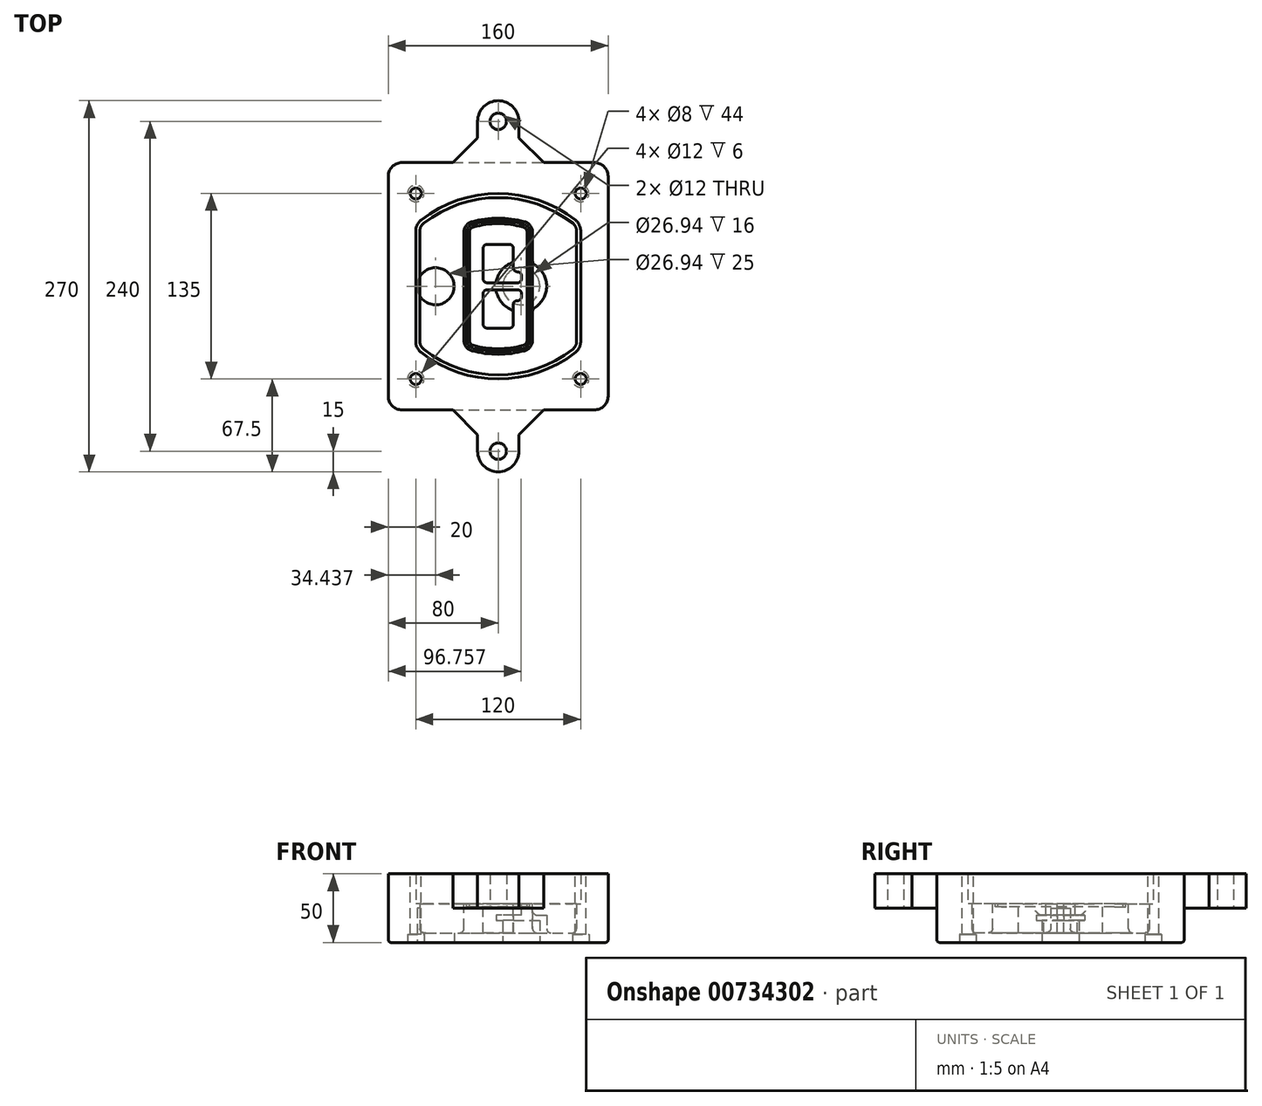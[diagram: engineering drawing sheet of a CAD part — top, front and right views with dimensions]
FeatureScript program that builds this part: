
annotation { "Feature Type Name" : "Feature", "Feature Type Description" : "" }
export const myFeature = defineFeature(function(context is Context, id is Id, definition is map)
    precondition{}
    {
        {
            var Q0;
            Q0=qCreatedBy(makeId("Top.planeOp"),FACE);
            var sketch = newSketch(context, id + "F0", { "sketchPlane" : qUnion([Q0])});
            skPoint(sketch, "E0.rect.middle", {"position": v(0, 0) * mm});
            skLineSegment(sketch, "E1.bottom", {"start": v(-70, -90) * mm, "end": v(70, -90) * mm});
            skLineSegment(sketch, "E1.top", {"start": v(-70, 90) * mm, "end": v(70, 90) * mm});
            skLineSegment(sketch, "E1.left", {"start": v(-80, -80) * mm, "end": v(-80, 80) * mm});
            skLineSegment(sketch, "E1.right", {"start": v(80, -80) * mm, "end": v(80, 80) * mm});
            skLineSegment(sketch, "E2", {"start": v(-80, 90) * mm, "end": v(80, -90) * mm, "construction": true});
            skLineSegment(sketch, "E3", {"start": v(80, 90) * mm, "end": v(-80, -90) * mm, "construction": true});
            skCircle(sketch, "E4", {"center": v(-60, 67.5) * mm, "radius": 4 * mm});
            skCircle(sketch, "E5", {"center": v(60, 67.5) * mm, "radius": 4 * mm});
            skCircle(sketch, "E6", {"center": v(60, -67.5) * mm, "radius": 4 * mm});
            skCircle(sketch, "E7", {"center": v(-60, -67.5) * mm, "radius": 4 * mm});
            skLineSegment(sketch, "E8", {"start": v(-60, 67.5) * mm, "end": v(60, 67.5) * mm, "construction": true});
            skLineSegment(sketch, "E9", {"start": v(60, 67.5) * mm, "end": v(60, -67.5) * mm, "construction": true});
            skLineSegment(sketch, "E10", {"start": v(60, -67.5) * mm, "end": v(-60, -67.5) * mm, "construction": true});
            skLineSegment(sketch, "E11", {"start": v(-60, -67.5) * mm, "end": v(-60, 67.5) * mm, "construction": true});
            skLineSegment(sketch, "E12", {"start": v(-60, 40.3) * mm, "end": v(-60, -40.3) * mm});
            skLineSegment(sketch, "E13", {"start": v(60, 40.3) * mm, "end": v(60, -40.3) * mm});
            skArc(sketch, "E14", {"start": v(56.15, 48.18) * mm, "mid": v(0, 67.5) * mm, "end": v(-56.15, 48.18) * mm});
            skArc(sketch, "E15", {"start": v(-56.15, -48.18) * mm, "mid": v(0, -67.5) * mm, "end": v(56.15, -48.18) * mm});
            skLineSegment(sketch, "E16", {"start": v(-60, 0) * mm, "end": v(60, 0) * mm, "construction": true});
            skPoint(sketch, "E17.visualSharp", {"position": v(-60, -45) * mm});
            skArc(sketch, "E17.filletArc", {"start": v(-60, -40.3) * mm, "mid": v(-58.99, -44.68) * mm, "end": v(-56.15, -48.18) * mm});
            skPoint(sketch, "E18.visualSharp", {"position": v(-60, 45) * mm});
            skArc(sketch, "E18.filletArc", {"start": v(-56.15, 48.18) * mm, "mid": v(-58.99, 44.68) * mm, "end": v(-60, 40.3) * mm});
            skPoint(sketch, "E19.visualSharp", {"position": v(60, 45) * mm});
            skArc(sketch, "E19.filletArc", {"start": v(60, 40.3) * mm, "mid": v(58.99, 44.68) * mm, "end": v(56.15, 48.18) * mm});
            skPoint(sketch, "E20.visualSharp", {"position": v(60, -45) * mm});
            skArc(sketch, "E20.filletArc", {"start": v(56.15, -48.18) * mm, "mid": v(58.99, -44.68) * mm, "end": v(60, -40.3) * mm});
            skPoint(sketch, "E21.visualSharp", {"position": v(-80, 90) * mm});
            skArc(sketch, "E21.filletArc", {"start": v(-70, 90) * mm, "mid": v(-77.07, 87.07) * mm, "end": v(-80, 80) * mm});
            skPoint(sketch, "E22.visualSharp", {"position": v(80, 90) * mm});
            skArc(sketch, "E22.filletArc", {"start": v(80, 80) * mm, "mid": v(77.07, 87.07) * mm, "end": v(70, 90) * mm});
            skPoint(sketch, "E23.visualSharp", {"position": v(80, -90) * mm});
            skArc(sketch, "E23.filletArc", {"start": v(70, -90) * mm, "mid": v(77.07, -87.07) * mm, "end": v(80, -80) * mm});
            skPoint(sketch, "E24.visualSharp", {"position": v(-80, -90) * mm});
            skArc(sketch, "E24.filletArc", {"start": v(-80, -80) * mm, "mid": v(-77.07, -87.07) * mm, "end": v(-70, -90) * mm});
            skArc(sketch, "E25.0", {"start": v(57, 40.3) * mm, "mid": v(56.3, 43.36) * mm, "end": v(54.3, 45.81) * mm});
            skLineSegment(sketch, "E25.1", {"start": v(57, 40.3) * mm, "end": v(57, -40.3) * mm});
            skArc(sketch, "E25.2", {"start": v(54.3, -45.81) * mm, "mid": v(56.3, -43.36) * mm, "end": v(57, -40.3) * mm});
            skArc(sketch, "E25.3", {"start": v(-54.3, -45.81) * mm, "mid": v(0, -64.5) * mm, "end": v(54.3, -45.81) * mm});
            skArc(sketch, "E25.4", {"start": v(-57, -40.3) * mm, "mid": v(-56.3, -43.36) * mm, "end": v(-54.3, -45.81) * mm});
            skArc(sketch, "E25.5", {"start": v(54.3, 45.81) * mm, "mid": v(0, 64.5) * mm, "end": v(-54.3, 45.81) * mm});
            skLineSegment(sketch, "E25.6", {"start": v(-57, 40.3) * mm, "end": v(-57, -40.3) * mm});
            skArc(sketch, "E25.7", {"start": v(-54.3, 45.81) * mm, "mid": v(-56.3, 43.36) * mm, "end": v(-57, 40.3) * mm});
            skArc(sketch, "E26.0", {"start": v(-58.62, 51.33) * mm, "mid": v(-62.58, 46.43) * mm, "end": v(-64, 40.3) * mm});
            skArc(sketch, "E26.1", {"start": v(58.62, 51.33) * mm, "mid": v(0, 71.5) * mm, "end": v(-58.62, 51.33) * mm});
            skArc(sketch, "E26.2", {"start": v(64, 40.3) * mm, "mid": v(62.58, 46.43) * mm, "end": v(58.62, 51.33) * mm});
            skLineSegment(sketch, "E26.3", {"start": v(64, 40.3) * mm, "end": v(64, -40.3) * mm});
            skArc(sketch, "E26.4", {"start": v(58.62, -51.33) * mm, "mid": v(62.58, -46.43) * mm, "end": v(64, -40.3) * mm});
            skLineSegment(sketch, "E26.5", {"start": v(-64, 40.3) * mm, "end": v(-64, -40.3) * mm});
            skArc(sketch, "E26.6", {"start": v(-58.62, -51.33) * mm, "mid": v(0, -71.5) * mm, "end": v(58.62, -51.33) * mm});
            skArc(sketch, "E26.7", {"start": v(-64, -40.3) * mm, "mid": v(-62.58, -46.43) * mm, "end": v(-58.62, -51.33) * mm});
            skSolve(sketch);
        }
        {
            var Q0;
            Q0=makeQuery(id+"F0.imprint","IMPRINT",FACE,{"disambiguationData":[TD([[makeQuery(id+"F0.imprint","IMPRINT",EDGE,{"derivedFrom":sQuery(id+"F0.wireOp",EDGE,"E1.bottom")}),1.0]])]});
            var Q1;
            Q1=makeQuery(id+"F0.imprint","IMPRINT",FACE,{"disambiguationData":[TD([[makeQuery(id+"F0.imprint","IMPRINT",EDGE,{"derivedFrom":sQuery(id+"F0.wireOp",EDGE,"E12")}),1.0]])]});
            var Q2;
            Q2=makeQuery(id+"F0.imprint","IMPRINT",FACE,{"disambiguationData":[TD([[makeQuery(id+"F0.imprint","IMPRINT",EDGE,{"derivedFrom":sQuery(id+"F0.wireOp",EDGE,"E25.0")}),1.0]])]});
            var Q3;
            Q3=makeQuery(id+"F0.imprint","IMPRINT",FACE,{"disambiguationData":[TD([[makeQuery(id+"F0.imprint","IMPRINT",EDGE,{"derivedFrom":sQuery(id+"F0.wireOp",EDGE,"E12")}),-1.0]])]});
            extrude(context, id + "F1", {"entities" : qUnion([Q0, Q1, Q2, Q3]), "oppositeDirection" : true, "depth" : 25 * mm});
        }
        {
            var Q0;
            Q0=makeQuery(id+"F0.imprint","IMPRINT",FACE,{"disambiguationData":[TD([[makeQuery(id+"F0.imprint","IMPRINT",EDGE,{"derivedFrom":sQuery(id+"F0.wireOp",EDGE,"E12")}),1.0]])]});
            extrude(context, id + "F2", {"entities" : qUnion([Q0]), "operationType" : NewBodyOperationType.ADD, "depth" : 3 * mm});
        }
        {
            var Q0;
            Q0=makeQuery(id+"F0.imprint","IMPRINT",FACE,{"disambiguationData":[TD([[makeQuery(id+"F0.imprint","IMPRINT",EDGE,{"derivedFrom":sQuery(id+"F0.wireOp",EDGE,"E25.0")}),1.0]])]});
            extrude(context, id + "F3", {"entities" : qUnion([Q0]), "operationType" : NewBodyOperationType.REMOVE, "oppositeDirection" : true, "depth" : 18 * mm});
        }
        {
            var Q0;
            Q0=makeQuery(id+"F2.opExtrude","CAP_FACE",FACE,{"disambiguationData":[OSD([sQuery(id+"F0.wireOp",EDGE,"E12"),sQuery(id+"F0.wireOp",EDGE,"E13"),sQuery(id+"F0.wireOp",EDGE,"E14"),sQuery(id+"F0.wireOp",EDGE,"E15"),sQuery(id+"F0.wireOp",EDGE,"E17.filletArc"),sQuery(id+"F0.wireOp",EDGE,"E18.filletArc"),sQuery(id+"F0.wireOp",EDGE,"E19.filletArc"),sQuery(id+"F0.wireOp",EDGE,"E20.filletArc"),sQuery(id+"F0.wireOp",EDGE,"E25.0"),sQuery(id+"F0.wireOp",EDGE,"E25.1"),sQuery(id+"F0.wireOp",EDGE,"E25.2"),sQuery(id+"F0.wireOp",EDGE,"E25.3"),sQuery(id+"F0.wireOp",EDGE,"E25.4"),sQuery(id+"F0.wireOp",EDGE,"E25.5"),sQuery(id+"F0.wireOp",EDGE,"E25.6"),sQuery(id+"F0.wireOp",EDGE,"E25.7")])],"isStart":false});
            var sketch = newSketch(context, id + "F4", { "sketchPlane" : qUnion([Q0])});
            skArc(sketch, "E27.0", {"start": v(-19.08, -46.97) * mm, "mid": v(0, -49.5) * mm, "end": v(19.08, -46.97) * mm});
            skArc(sketch, "E28.0", {"start": v(19.08, 46.97) * mm, "mid": v(0, 49.5) * mm, "end": v(-19.08, 46.97) * mm});
            skLineSegment(sketch, "E29", {"start": v(-25, 39.25) * mm, "end": v(-25, -39.25) * mm});
            skLineSegment(sketch, "E30", {"start": v(25, 39.25) * mm, "end": v(25, -39.25) * mm});
            skLineSegment(sketch, "E31", {"start": v(-25, 45.1) * mm, "end": v(25, 45.1) * mm, "construction": true});
            skLineSegment(sketch, "E32", {"start": v(-25, -45.1) * mm, "end": v(25, -45.1) * mm, "construction": true});
            skPoint(sketch, "E33.visualSharp", {"position": v(-25, 45.1) * mm});
            skArc(sketch, "E33.filletArc", {"start": v(-19.08, 46.97) * mm, "mid": v(-23.35, 44.11) * mm, "end": v(-25, 39.25) * mm});
            skPoint(sketch, "E34.visualSharp", {"position": v(25, 45.1) * mm});
            skArc(sketch, "E34.filletArc", {"start": v(25, 39.25) * mm, "mid": v(23.35, 44.11) * mm, "end": v(19.08, 46.97) * mm});
            skPoint(sketch, "E35.visualSharp", {"position": v(25, -45.1) * mm});
            skArc(sketch, "E35.filletArc", {"start": v(19.08, -46.97) * mm, "mid": v(23.35, -44.11) * mm, "end": v(25, -39.25) * mm});
            skPoint(sketch, "E36.visualSharp", {"position": v(-25, -45.1) * mm});
            skArc(sketch, "E36.filletArc", {"start": v(-25, -39.25) * mm, "mid": v(-23.35, -44.11) * mm, "end": v(-19.08, -46.97) * mm});
            skArc(sketch, "E37.0", {"start": v(54.3, 45.81) * mm, "mid": v(0, 64.5) * mm, "end": v(-54.3, 45.81) * mm});
            skArc(sketch, "E37.1", {"start": v(-54.3, 45.81) * mm, "mid": v(-56.3, 43.36) * mm, "end": v(-57, 40.3) * mm});
            skLineSegment(sketch, "E37.2", {"start": v(-57, 40.3) * mm, "end": v(-57, -40.3) * mm});
            skArc(sketch, "E37.3", {"start": v(-57, -40.3) * mm, "mid": v(-56.3, -43.36) * mm, "end": v(-54.3, -45.81) * mm});
            skArc(sketch, "E37.4", {"start": v(-54.3, -45.81) * mm, "mid": v(0, -64.5) * mm, "end": v(54.3, -45.81) * mm});
            skArc(sketch, "E37.5", {"start": v(54.3, -45.81) * mm, "mid": v(56.3, -43.36) * mm, "end": v(57, -40.3) * mm});
            skLineSegment(sketch, "E37.6", {"start": v(57, 40.3) * mm, "end": v(57, -40.3) * mm});
            skArc(sketch, "E37.7", {"start": v(57, 40.3) * mm, "mid": v(56.3, 43.36) * mm, "end": v(54.3, 45.81) * mm});
            skLineSegment(sketch, "E38.0", {"start": v(23, 39.25) * mm, "end": v(23, -39.25) * mm});
            skArc(sketch, "E38.1", {"start": v(18.56, -45.04) * mm, "mid": v(21.76, -42.9) * mm, "end": v(23, -39.25) * mm});
            skArc(sketch, "E38.2", {"start": v(-18.56, -45.04) * mm, "mid": v(0, -47.5) * mm, "end": v(18.56, -45.04) * mm});
            skArc(sketch, "E38.3", {"start": v(-23, -39.25) * mm, "mid": v(-21.76, -42.9) * mm, "end": v(-18.56, -45.04) * mm});
            skLineSegment(sketch, "E38.4", {"start": v(-23, 39.25) * mm, "end": v(-23, -39.25) * mm});
            skArc(sketch, "E38.5", {"start": v(23, 39.25) * mm, "mid": v(21.76, 42.9) * mm, "end": v(18.56, 45.04) * mm});
            skArc(sketch, "E38.6", {"start": v(-18.56, 45.04) * mm, "mid": v(-21.76, 42.9) * mm, "end": v(-23, 39.25) * mm});
            skArc(sketch, "E38.7", {"start": v(18.56, 45.04) * mm, "mid": v(0, 47.5) * mm, "end": v(-18.56, 45.04) * mm});
            skArc(sketch, "E39.0", {"start": v(21, 39.25) * mm, "mid": v(20.18, 41.68) * mm, "end": v(18.04, 43.1) * mm});
            skLineSegment(sketch, "E39.1", {"start": v(21, 39.25) * mm, "end": v(21, -39.25) * mm});
            skArc(sketch, "E39.2", {"start": v(18.04, -43.1) * mm, "mid": v(20.18, -41.68) * mm, "end": v(21, -39.25) * mm});
            skArc(sketch, "E39.3", {"start": v(-18.04, -43.1) * mm, "mid": v(0, -45.5) * mm, "end": v(18.04, -43.1) * mm});
            skArc(sketch, "E39.4", {"start": v(-21, -39.25) * mm, "mid": v(-20.18, -41.68) * mm, "end": v(-18.04, -43.1) * mm});
            skArc(sketch, "E39.5", {"start": v(18.04, 43.1) * mm, "mid": v(0, 45.5) * mm, "end": v(-18.04, 43.1) * mm});
            skLineSegment(sketch, "E39.6", {"start": v(-21, 39.25) * mm, "end": v(-21, -39.25) * mm});
            skArc(sketch, "E39.7", {"start": v(-18.04, 43.1) * mm, "mid": v(-20.18, 41.68) * mm, "end": v(-21, 39.25) * mm});
            skLineSegment(sketch, "E40", {"start": v(-25, 0) * mm, "end": v(25, 0) * mm, "construction": true});
            skLineSegment(sketch, "E41", {"start": v(-11, 5.5) * mm, "end": v(-11, 27.5) * mm});
            skLineSegment(sketch, "E42", {"start": v(-8, 30.5) * mm, "end": v(8, 30.5) * mm});
            skLineSegment(sketch, "E43", {"start": v(11, 27.5) * mm, "end": v(11, 13.5) * mm});
            skLineSegment(sketch, "E44", {"start": v(14, 10.5) * mm, "end": v(14, 10.5) * mm});
            skLineSegment(sketch, "E45", {"start": v(17, 7.5) * mm, "end": v(17, 5.5) * mm});
            skLineSegment(sketch, "E46", {"start": v(14, 2.5) * mm, "end": v(-8, 2.5) * mm});
            skPoint(sketch, "E47.visualSharp", {"position": v(-11, 30.5) * mm});
            skArc(sketch, "E47.filletArc", {"start": v(-8, 30.5) * mm, "mid": v(-10.12, 29.62) * mm, "end": v(-11, 27.5) * mm});
            skPoint(sketch, "E48.visualSharp", {"position": v(11, 30.5) * mm});
            skArc(sketch, "E48.filletArc", {"start": v(11, 27.5) * mm, "mid": v(10.12, 29.62) * mm, "end": v(8, 30.5) * mm});
            skPoint(sketch, "E49.visualSharp", {"position": v(11, 10.5) * mm});
            skArc(sketch, "E49.filletArc", {"start": v(11, 13.5) * mm, "mid": v(11.88, 11.38) * mm, "end": v(14, 10.5) * mm});
            skPoint(sketch, "E50.visualSharp", {"position": v(17, 10.5) * mm});
            skArc(sketch, "E50.filletArc", {"start": v(17, 7.5) * mm, "mid": v(16.12, 9.62) * mm, "end": v(14, 10.5) * mm});
            skPoint(sketch, "E51.visualSharp", {"position": v(17, 2.5) * mm});
            skArc(sketch, "E51.filletArc", {"start": v(14, 2.5) * mm, "mid": v(16.12, 3.38) * mm, "end": v(17, 5.5) * mm});
            skPoint(sketch, "E52.visualSharp", {"position": v(-11, 2.5) * mm});
            skArc(sketch, "E52.filletArc", {"start": v(-11, 5.5) * mm, "mid": v(-10.12, 3.38) * mm, "end": v(-8, 2.5) * mm});
            skLineSegment(sketch, "E53.0.MirrorCS", {"start": v(14, -2.5) * mm, "end": v(-8, -2.5) * mm});
            skArc(sketch, "E54.0.MirrorCS", {"start": v(-11, -5.5) * mm, "mid": v(-10.12, -3.38) * mm, "end": v(-8, -2.5) * mm});
            skLineSegment(sketch, "E55.0.MirrorCS", {"start": v(-11, -5.5) * mm, "end": v(-11, -27.5) * mm});
            skArc(sketch, "E56.0.MirrorCS", {"start": v(-8, -30.5) * mm, "mid": v(-10.12, -29.62) * mm, "end": v(-11, -27.5) * mm});
            skLineSegment(sketch, "E57.0.MirrorCS", {"start": v(-8, -30.5) * mm, "end": v(8, -30.5) * mm});
            skArc(sketch, "E58.0.MirrorCS", {"start": v(11, -27.5) * mm, "mid": v(10.12, -29.62) * mm, "end": v(8, -30.5) * mm});
            skLineSegment(sketch, "E59.0.MirrorCS", {"start": v(11, -27.5) * mm, "end": v(11, -13.5) * mm});
            skArc(sketch, "E60.0.MirrorCS", {"start": v(11, -13.5) * mm, "mid": v(11.88, -11.38) * mm, "end": v(14, -10.5) * mm});
            skArc(sketch, "E61.0.MirrorCS", {"start": v(17, -7.5) * mm, "mid": v(16.12, -9.62) * mm, "end": v(14, -10.5) * mm});
            skLineSegment(sketch, "E62.0.MirrorCS", {"start": v(17, -7.5) * mm, "end": v(17, -5.5) * mm});
            skArc(sketch, "E63.0.MirrorCS", {"start": v(14, -2.5) * mm, "mid": v(16.12, -3.38) * mm, "end": v(17, -5.5) * mm});
            skSolve(sketch);
        }
        {
            var Q0;
            Q0=makeQuery(id+"F4.imprint","IMPRINT",FACE,{"disambiguationData":[TD([[makeQuery(id+"F4.imprint","IMPRINT",EDGE,{"derivedFrom":sQuery(id+"F4.wireOp",EDGE,"E27.0")}),1.0]])]});
            var Q1;
            Q1=makeQuery(id+"F4.imprint","IMPRINT",FACE,{"disambiguationData":[TD([[makeQuery(id+"F4.imprint","IMPRINT",EDGE,{"derivedFrom":sQuery(id+"F4.wireOp",EDGE,"E38.0")}),-1.0]])]});
            var Q2;
            Q2=makeQuery(id+"F4.imprint","IMPRINT",FACE,{"disambiguationData":[TD([[makeQuery(id+"F4.imprint","IMPRINT",EDGE,{"derivedFrom":sQuery(id+"F4.wireOp",EDGE,"E39.0")}),1.0]])]});
            extrude(context, id + "F5", {"entities" : qUnion([Q0, Q1, Q2]), "operationType" : NewBodyOperationType.ADD, "endBound" : BoundingType.UP_TO_NEXT, "oppositeDirection" : true, "depth" : 25 * mm});
        }
        {
            var Q0;
            Q0=makeQuery(id+"F4.imprint","IMPRINT",FACE,{"disambiguationData":[TD([[makeQuery(id+"F4.imprint","IMPRINT",EDGE,{"derivedFrom":sQuery(id+"F4.wireOp",EDGE,"E38.0")}),-1.0]])]});
            extrude(context, id + "F6", {"entities" : qUnion([Q0]), "operationType" : NewBodyOperationType.REMOVE, "oppositeDirection" : true, "depth" : 2 * mm});
        }
        {
            var Q0;
            Q0=makeQuery(id+"F1.opExtrude","CAP_FACE",FACE,{"disambiguationData":[OSD([sQuery(id+"F0.wireOp",EDGE,"E1.bottom"),sQuery(id+"F0.wireOp",EDGE,"E1.top"),sQuery(id+"F0.wireOp",EDGE,"E1.left"),sQuery(id+"F0.wireOp",EDGE,"E1.right"),sQuery(id+"F0.wireOp",EDGE,"E4"),sQuery(id+"F0.wireOp",EDGE,"E5"),sQuery(id+"F0.wireOp",EDGE,"E6"),sQuery(id+"F0.wireOp",EDGE,"E7"),sQuery(id+"F0.wireOp",EDGE,"E21.filletArc"),sQuery(id+"F0.wireOp",EDGE,"E22.filletArc"),sQuery(id+"F0.wireOp",EDGE,"E23.filletArc"),sQuery(id+"F0.wireOp",EDGE,"E24.filletArc")])],"isStart":false});
            var sketch = newSketch(context, id + "F7", { "sketchPlane" : qUnion([Q0])});
            skCircle(sketch, "E64", {"center": v(16.76, 0) * mm, "radius": 13.47 * mm});
            skCircle(sketch, "E65", {"center": v(-45.56, 0) * mm, "radius": 13.47 * mm});
            skLineSegment(sketch, "E66", {"start": v(80, 0) * mm, "end": v(-80, 0) * mm});
            skCircle(sketch, "E67", {"center": v(16.76, 0) * mm, "radius": 18.47 * mm});
            skCircle(sketch, "E68", {"center": v(60, -67.5) * mm, "radius": 6 * mm});
            skCircle(sketch, "E69", {"center": v(-60, -67.5) * mm, "radius": 6 * mm});
            skCircle(sketch, "E70", {"center": v(-60, 67.5) * mm, "radius": 6 * mm});
            skCircle(sketch, "E71", {"center": v(60, 67.5) * mm, "radius": 6 * mm});
            skSolve(sketch);
        }
        {
            var Q0;
            {var subQ1=sQuery(id+"F7.wireOp",EDGE,"E66");var subQ4=sQuery(id+"F7.wireOp",EDGE,"E64");var subQ6=makeQuery(id+"F7.imprint","INTERSECT",VERTEX,{"disambiguationData":[OD(0.0)],"derivedFrom":[subQ4,subQ1]});Q0=makeQuery(id+"F7.imprint","IMPRINT",FACE,{"disambiguationData":[TD([[makeQuery(id+"F7.imprint","IMPRINT",EDGE,{"disambiguationData":[TD([[subQ6,-1.0]])],"derivedFrom":subQ4}),-1.0]])]});}
            var Q1;
            {var subQ0=sQuery(id+"F7.wireOp",EDGE,"E66");var subQ1=sQuery(id+"F7.wireOp",EDGE,"E64");var subQ3=makeQuery(id+"F7.imprint","INTERSECT",VERTEX,{"disambiguationData":[OD(0.0)],"derivedFrom":[subQ1,subQ0]});Q1=makeQuery(id+"F7.imprint","IMPRINT",FACE,{"disambiguationData":[TD([[makeQuery(id+"F7.imprint","IMPRINT",EDGE,{"disambiguationData":[TD([[subQ3,-1.0]])],"derivedFrom":subQ1}),1.0]])]});}
            var Q2;
            {var subQ0=sQuery(id+"F7.wireOp",EDGE,"E66");var subQ1=sQuery(id+"F7.wireOp",EDGE,"E64");var subQ3=makeQuery(id+"F7.imprint","INTERSECT",VERTEX,{"disambiguationData":[OD(0.0)],"derivedFrom":[subQ1,subQ0]});Q2=makeQuery(id+"F7.imprint","IMPRINT",FACE,{"disambiguationData":[TD([[makeQuery(id+"F7.imprint","IMPRINT",EDGE,{"disambiguationData":[TD([[subQ3,1.0]])],"derivedFrom":subQ1}),1.0]])]});}
            var Q3;
            {var subQ1=sQuery(id+"F7.wireOp",EDGE,"E66");var subQ4=sQuery(id+"F7.wireOp",EDGE,"E64");var subQ6=makeQuery(id+"F7.imprint","INTERSECT",VERTEX,{"disambiguationData":[OD(0.0)],"derivedFrom":[subQ4,subQ1]});Q3=makeQuery(id+"F7.imprint","IMPRINT",FACE,{"disambiguationData":[TD([[makeQuery(id+"F7.imprint","IMPRINT",EDGE,{"disambiguationData":[TD([[subQ6,1.0]])],"derivedFrom":subQ4}),-1.0]])]});}
            extrude(context, id + "F8", {"entities" : qUnion([Q0, Q1, Q2, Q3]), "operationType" : NewBodyOperationType.ADD, "oppositeDirection" : true, "depth" : 20 * mm});
        }
        {
            var Q0;
            {var subQ0=sQuery(id+"F7.wireOp",EDGE,"E66");var subQ1=sQuery(id+"F7.wireOp",EDGE,"E64");var subQ3=makeQuery(id+"F7.imprint","INTERSECT",VERTEX,{"disambiguationData":[OD(0.0)],"derivedFrom":[subQ1,subQ0]});Q0=makeQuery(id+"F7.imprint","IMPRINT",FACE,{"disambiguationData":[TD([[makeQuery(id+"F7.imprint","IMPRINT",EDGE,{"disambiguationData":[TD([[subQ3,-1.0]])],"derivedFrom":subQ1}),1.0]])]});}
            var Q1;
            {var subQ0=sQuery(id+"F7.wireOp",EDGE,"E66");var subQ1=sQuery(id+"F7.wireOp",EDGE,"E64");var subQ3=makeQuery(id+"F7.imprint","INTERSECT",VERTEX,{"disambiguationData":[OD(0.0)],"derivedFrom":[subQ1,subQ0]});Q1=makeQuery(id+"F7.imprint","IMPRINT",FACE,{"disambiguationData":[TD([[makeQuery(id+"F7.imprint","IMPRINT",EDGE,{"disambiguationData":[TD([[subQ3,1.0]])],"derivedFrom":subQ1}),1.0]])]});}
            extrude(context, id + "F9", {"entities" : qUnion([Q0, Q1]), "operationType" : NewBodyOperationType.REMOVE, "oppositeDirection" : true, "depth" : 16 * mm});
        }
        {
            var Q0;
            {var subQ0=sQuery(id+"F7.wireOp",EDGE,"E66");var subQ1=sQuery(id+"F7.wireOp",EDGE,"E65");var subQ3=makeQuery(id+"F7.imprint","INTERSECT",VERTEX,{"disambiguationData":[OD(0.0)],"derivedFrom":[subQ1,subQ0]});Q0=makeQuery(id+"F7.imprint","IMPRINT",FACE,{"disambiguationData":[TD([[makeQuery(id+"F7.imprint","IMPRINT",EDGE,{"disambiguationData":[TD([[subQ3,-1.0]])],"derivedFrom":subQ1}),1.0]])]});}
            var Q1;
            {var subQ0=sQuery(id+"F7.wireOp",EDGE,"E66");var subQ1=sQuery(id+"F7.wireOp",EDGE,"E65");var subQ3=makeQuery(id+"F7.imprint","INTERSECT",VERTEX,{"disambiguationData":[OD(0.0)],"derivedFrom":[subQ1,subQ0]});Q1=makeQuery(id+"F7.imprint","IMPRINT",FACE,{"disambiguationData":[TD([[makeQuery(id+"F7.imprint","IMPRINT",EDGE,{"disambiguationData":[TD([[subQ3,1.0]])],"derivedFrom":subQ1}),1.0]])]});}
            extrude(context, id + "F10", {"entities" : qUnion([Q0, Q1]), "operationType" : NewBodyOperationType.REMOVE, "oppositeDirection" : true, "depth" : 25 * mm});
        }
        {
            var Q0;
            Q0=makeQuery(id+"F7.imprint","IMPRINT",FACE,{"disambiguationData":[TD([[makeQuery(id+"F7.imprint","IMPRINT",EDGE,{"derivedFrom":sQuery(id+"F7.wireOp",EDGE,"E68")}),1.0]])]});
            var Q1;
            Q1=makeQuery(id+"F7.imprint","IMPRINT",FACE,{"disambiguationData":[TD([[makeQuery(id+"F7.imprint","IMPRINT",EDGE,{"derivedFrom":makeQuery(id+"F1.opExtrude","CAP_EDGE",EDGE,{"disambiguationData":[OSD([sQuery(id+"F0.wireOp",EDGE,"E5")])],"isStart":false})}),-1.0]])]});
            var Q2;
            Q2=makeQuery(id+"F7.imprint","IMPRINT",FACE,{"disambiguationData":[TD([[makeQuery(id+"F7.imprint","IMPRINT",EDGE,{"derivedFrom":sQuery(id+"F7.wireOp",EDGE,"E69")}),1.0]])]});
            var Q3;
            Q3=makeQuery(id+"F7.imprint","IMPRINT",FACE,{"disambiguationData":[TD([[makeQuery(id+"F7.imprint","IMPRINT",EDGE,{"derivedFrom":makeQuery(id+"F1.opExtrude","CAP_EDGE",EDGE,{"disambiguationData":[OSD([sQuery(id+"F0.wireOp",EDGE,"E4")])],"isStart":false})}),-1.0]])]});
            var Q4;
            Q4=makeQuery(id+"F7.imprint","IMPRINT",FACE,{"disambiguationData":[TD([[makeQuery(id+"F7.imprint","IMPRINT",EDGE,{"derivedFrom":sQuery(id+"F7.wireOp",EDGE,"E70")}),1.0]])]});
            var Q5;
            Q5=makeQuery(id+"F7.imprint","IMPRINT",FACE,{"disambiguationData":[TD([[makeQuery(id+"F7.imprint","IMPRINT",EDGE,{"derivedFrom":makeQuery(id+"F1.opExtrude","CAP_EDGE",EDGE,{"disambiguationData":[OSD([sQuery(id+"F0.wireOp",EDGE,"E7")])],"isStart":false})}),-1.0]])]});
            var Q6;
            Q6=makeQuery(id+"F7.imprint","IMPRINT",FACE,{"disambiguationData":[TD([[makeQuery(id+"F7.imprint","IMPRINT",EDGE,{"derivedFrom":sQuery(id+"F7.wireOp",EDGE,"E71")}),1.0]])]});
            var Q7;
            Q7=makeQuery(id+"F7.imprint","IMPRINT",FACE,{"disambiguationData":[TD([[makeQuery(id+"F7.imprint","IMPRINT",EDGE,{"derivedFrom":makeQuery(id+"F1.opExtrude","CAP_EDGE",EDGE,{"disambiguationData":[OSD([sQuery(id+"F0.wireOp",EDGE,"E6")])],"isStart":false})}),-1.0]])]});
            extrude(context, id + "F11", {"entities" : qUnion([Q0, Q1, Q2, Q3, Q4, Q5, Q6, Q7]), "operationType" : NewBodyOperationType.REMOVE, "oppositeDirection" : true, "depth" : 6 * mm});
        }
        {
            var Q0;
            Q0=makeQuery(id+"F9.boolean.opBoolean","COPY",FACE,{"derivedFrom":makeQuery(id+"F9.opExtrude","CAP_FACE",FACE,{"disambiguationData":[OSD([sQuery(id+"F7.wireOp",EDGE,"E64")])],"isStart":false})});
            var sketch = newSketch(context, id + "F12", { "sketchPlane" : qUnion([Q0])});
            skArc(sketch, "E72.0", {"start": v(11, 17.55) * mm, "mid": v(2.57, 11.82) * mm, "end": v(-1.54, 2.5) * mm});
            skArc(sketch, "E72.1", {"start": v(-1.54, -2.5) * mm, "mid": v(2.57, -11.82) * mm, "end": v(11, -17.55) * mm});
            skLineSegment(sketch, "E73", {"start": v(-1.54, -2.5) * mm, "end": v(14, -2.5) * mm});
            skLineSegment(sketch, "E74.0", {"start": v(14, 2.5) * mm, "end": v(-1.54, 2.5) * mm});
            skArc(sketch, "E74.1", {"start": v(14, 2.5) * mm, "mid": v(16.12, 3.38) * mm, "end": v(17, 5.5) * mm});
            skLineSegment(sketch, "E74.2", {"start": v(17, 7.5) * mm, "end": v(17, 5.5) * mm});
            skArc(sketch, "E74.3", {"start": v(17, 7.5) * mm, "mid": v(16.12, 9.62) * mm, "end": v(14, 10.5) * mm});
            skArc(sketch, "E74.4", {"start": v(11, 13.5) * mm, "mid": v(11.88, 11.38) * mm, "end": v(14, 10.5) * mm});
            skLineSegment(sketch, "E74.5", {"start": v(11, 17.55) * mm, "end": v(11, 13.5) * mm});
            skLineSegment(sketch, "E74.7", {"start": v(14, -2.5) * mm, "end": v(-1.54, -2.5) * mm});
            skArc(sketch, "E74.8", {"start": v(14, -2.5) * mm, "mid": v(16.12, -3.38) * mm, "end": v(17, -5.5) * mm});
            skLineSegment(sketch, "E74.9", {"start": v(17, -7.5) * mm, "end": v(17, -5.5) * mm});
            skArc(sketch, "E74.10", {"start": v(17, -7.5) * mm, "mid": v(16.12, -9.62) * mm, "end": v(14, -10.5) * mm});
            skArc(sketch, "E74.11", {"start": v(11, -13.5) * mm, "mid": v(11.88, -11.38) * mm, "end": v(14, -10.5) * mm});
            skLineSegment(sketch, "E74.12", {"start": v(11, -17.55) * mm, "end": v(11, -13.5) * mm});
            skPoint(sketch, "E75.orphan", {"position": v(11, -27.5) * mm});
            skPoint(sketch, "E76.orphan", {"position": v(-8, -2.5) * mm});
            skPoint(sketch, "E77.orphan", {"position": v(-8, 2.5) * mm});
            skPoint(sketch, "E78.orphan", {"position": v(11, 27.5) * mm});
            skSolve(sketch);
        }
        {
            var Q0;
            {var subQ7=sQuery(id+"F12.wireOp",EDGE,"E72.0");var subQ14=sQuery(id+"F12.wireOp",EDGE,"E72.1");var subQ16=sQuery(id+"F12.wireOp",EDGE,"E74.1");var subQ18=sQuery(id+"F12.wireOp",EDGE,"E74.8");Q0=qUnion([makeQuery(id+"F12.imprint","IMPRINT",FACE,{"disambiguationData":[TD([[makeQuery(id+"F12.imprint","IMPRINT",EDGE,{"derivedFrom":subQ7}),1.0]])]}),makeQuery(id+"F12.imprint","IMPRINT",FACE,{"disambiguationData":[TD([[makeQuery(id+"F12.imprint","IMPRINT",EDGE,{"derivedFrom":subQ14}),1.0]])]}),makeQuery(id+"F12.imprint","IMPRINT",FACE,{"disambiguationData":[TD([[makeQuery(id+"F12.imprint","IMPRINT",EDGE,{"derivedFrom":subQ16}),1.0]])]}),makeQuery(id+"F12.imprint","IMPRINT",FACE,{"disambiguationData":[TD([[makeQuery(id+"F12.imprint","IMPRINT",EDGE,{"derivedFrom":subQ18}),-1.0]])]})]);}
            var Q1;
            Q1=makeQuery(id+"F5.boolean.opBoolean","SPLIT",FACE,{"disambiguationData":[TD([makeQuery(id+"F5.opExtrude","SWEPT_FACE",FACE,{"disambiguationData":[OSD([sQuery(id+"F4.wireOp",EDGE,"E41")])]})])],"derivedFrom":makeQuery(id+"F3.boolean.opBoolean","COPY",FACE,{"derivedFrom":makeQuery(id+"F3.opExtrude","CAP_FACE",FACE,{"disambiguationData":[OSD([sQuery(id+"F0.wireOp",EDGE,"E25.0"),sQuery(id+"F0.wireOp",EDGE,"E25.1"),sQuery(id+"F0.wireOp",EDGE,"E25.2"),sQuery(id+"F0.wireOp",EDGE,"E25.3"),sQuery(id+"F0.wireOp",EDGE,"E25.4"),sQuery(id+"F0.wireOp",EDGE,"E25.5"),sQuery(id+"F0.wireOp",EDGE,"E25.6"),sQuery(id+"F0.wireOp",EDGE,"E25.7")])],"isStart":false})})});
            extrude(context, id + "F13", {"entities" : qUnion([Q0]), "operationType" : NewBodyOperationType.REMOVE, "endBound" : BoundingType.UP_TO_SURFACE, "endBoundEntityFace" : qUnion([Q1]), "depth" : 25 * mm});
        }
        {
            var Q0;
            Q0=makeQuery(id+"F3.boolean.opBoolean","COPY",EDGE,{"derivedFrom":makeQuery(id+"F3.opExtrude","CAP_EDGE",EDGE,{"disambiguationData":[OSD([sQuery(id+"F0.wireOp",EDGE,"E25.6")])],"isStart":false})});
            var Q1;
            Q1=makeQuery(id+"F8.boolean.opBoolean","INTERSECT",EDGE,{"derivedFrom":[makeQuery(id+"F5.opExtrude","SWEPT_FACE",FACE,{"disambiguationData":[OSD([sQuery(id+"F4.wireOp",EDGE,"E30")])]}),makeQuery(id+"F8.opExtrude","CAP_FACE",FACE,{"disambiguationData":[OSD([sQuery(id+"F7.wireOp",EDGE,"E67")])],"isStart":false})]});
            var Q2;
            Q2=makeQuery(id+"F8.boolean.opBoolean","INTERSECT",EDGE,{"disambiguationData":[OD(1.0)],"derivedFrom":[makeQuery(id+"F5.opExtrude","SWEPT_FACE",FACE,{"disambiguationData":[OSD([sQuery(id+"F4.wireOp",EDGE,"E30")])]}),makeQuery(id+"F8.opExtrude","SWEPT_FACE",FACE,{"disambiguationData":[OSD([sQuery(id+"F7.wireOp",EDGE,"E67")])]})]});
            var Q3;
            {var subQ0=sQuery(id+"F4.wireOp",EDGE,"E30");Q3=makeQuery(id+"F8.boolean.opBoolean","SPLIT",EDGE,{"disambiguationData":[TD([makeQuery(id+"F5.opExtrude","SWEPT_FACE",FACE,{"disambiguationData":[OSD([sQuery(id+"F4.wireOp",EDGE,"E35.filletArc")])]})])],"derivedFrom":makeQuery(id+"F5.opExtrude","CAP_EDGE",EDGE,{"disambiguationData":[OSD([subQ0])],"isStart":false})});}
            var Q4;
            {var subQ0=sQuery(id+"F0.wireOp",EDGE,"E25.7");var subQ1=sQuery(id+"F0.wireOp",EDGE,"E25.1");var subQ2=sQuery(id+"F0.wireOp",EDGE,"E25.6");var subQ3=sQuery(id+"F0.wireOp",EDGE,"E25.5");var subQ4=sQuery(id+"F0.wireOp",EDGE,"E25.4");var subQ5=sQuery(id+"F0.wireOp",EDGE,"E25.0");var subQ6=sQuery(id+"F0.wireOp",EDGE,"E25.2");var subQ7=sQuery(id+"F0.wireOp",EDGE,"E25.3");Q4=makeQuery(id+"F8.boolean.opBoolean","INTERSECT",EDGE,{"derivedFrom":[makeQuery(id+"F5.boolean.opBoolean","SPLIT",FACE,{"disambiguationData":[TD([makeQuery(id+"F2.opExtrude","SWEPT_FACE",FACE,{"disambiguationData":[OSD([subQ5])]})])],"derivedFrom":makeQuery(id+"F3.boolean.opBoolean","COPY",FACE,{"derivedFrom":makeQuery(id+"F3.opExtrude","CAP_FACE",FACE,{"disambiguationData":[OSD([subQ5,subQ1,subQ6,subQ7,subQ4,subQ3,subQ2,subQ0])],"isStart":false})})}),makeQuery(id+"F8.opExtrude","SWEPT_FACE",FACE,{"disambiguationData":[OSD([sQuery(id+"F7.wireOp",EDGE,"E67")])]})]});}
            var Q5;
            Q5=makeQuery(id+"F8.boolean.opBoolean","INTERSECT",EDGE,{"disambiguationData":[OD(0.0)],"derivedFrom":[makeQuery(id+"F5.opExtrude","SWEPT_FACE",FACE,{"disambiguationData":[OSD([sQuery(id+"F4.wireOp",EDGE,"E30")])]}),makeQuery(id+"F8.opExtrude","SWEPT_FACE",FACE,{"disambiguationData":[OSD([sQuery(id+"F7.wireOp",EDGE,"E67")])]})]});
            fillet(context, id + "F14", {"entities" : qUnion([Q0, Q1, Q2, Q3, Q4, Q5]), "radius" : 3 * mm, "tangentPropagation" : true, "allowEdgeOverflow" : false});
        }
        {
            var Q0;
            Q0=makeQuery(id+"F1.opExtrude","CAP_EDGE",EDGE,{"disambiguationData":[OSD([sQuery(id+"F0.wireOp",EDGE,"E1.bottom")])],"isStart":false});
            fillet(context, id + "F15", {"entities" : qUnion([Q0]), "radius" : 2 * mm, "tangentPropagation" : true, "allowEdgeOverflow" : false});
        }
        {
            var Q0;
            {var subQ0=sQuery(id+"F0.wireOp",EDGE,"E21.filletArc");var subQ1=sQuery(id+"F0.wireOp",EDGE,"E7");var subQ2=sQuery(id+"F0.wireOp",EDGE,"E6");var subQ3=sQuery(id+"F0.wireOp",EDGE,"E5");var subQ4=sQuery(id+"F0.wireOp",EDGE,"E4");var subQ5=sQuery(id+"F0.wireOp",EDGE,"E22.filletArc");var subQ6=sQuery(id+"F0.wireOp",EDGE,"E1.bottom");var subQ7=sQuery(id+"F0.wireOp",EDGE,"E1.right");var subQ8=sQuery(id+"F0.wireOp",EDGE,"E1.top");var subQ9=sQuery(id+"F0.wireOp",EDGE,"E1.left");var subQ10=sQuery(id+"F0.wireOp",EDGE,"E23.filletArc");var subQ11=sQuery(id+"F0.wireOp",EDGE,"E24.filletArc");Q0=makeQuery(id+"F2.boolean.opBoolean","SPLIT",FACE,{"disambiguationData":[TD([makeQuery(id+"F1.opExtrude","SWEPT_FACE",FACE,{"disambiguationData":[OSD([subQ6])]})])],"derivedFrom":makeQuery(id+"F1.opExtrude","CAP_FACE",FACE,{"disambiguationData":[OSD([subQ6,subQ8,subQ9,subQ7,subQ4,subQ3,subQ2,subQ1,subQ0,subQ5,subQ10,subQ11])],"isStart":true})});}
            var sketch = newSketch(context, id + "F16", { "sketchPlane" : qUnion([Q0])});
            skLineSegment(sketch, "E79", {"start": v(0, 90) * mm, "end": v(0, 120) * mm, "construction": true});
            skLineSegment(sketch, "E80", {"start": v(-33, 90) * mm, "end": v(-15, 108) * mm});
            skLineSegment(sketch, "E81", {"start": v(-15, 108) * mm, "end": v(-15, 120) * mm});
            skLineSegment(sketch, "E82", {"start": v(15, 108) * mm, "end": v(15, 120) * mm});
            skArc(sketch, "E83", {"start": v(15, 120) * mm, "mid": v(0, 135) * mm, "end": v(-15, 120) * mm});
            skCircle(sketch, "E84", {"center": v(0, 120) * mm, "radius": 6 * mm});
            skLineSegment(sketch, "E85", {"start": v(15, 108) * mm, "end": v(33, 90) * mm});
            skLineSegment(sketch, "E86", {"start": v(80, 0) * mm, "end": v(-80, 0) * mm, "construction": true});
            skLineSegment(sketch, "E87.MirrorCS", {"start": v(15, -108) * mm, "end": v(33, -90) * mm});
            skLineSegment(sketch, "E88.MirrorCS", {"start": v(15, -108) * mm, "end": v(15, -120) * mm});
            skArc(sketch, "E89.MirrorCS", {"start": v(15, -120) * mm, "mid": v(0, -135) * mm, "end": v(-15, -120) * mm});
            skCircle(sketch, "E90.MirrorC", {"center": v(0, -120) * mm, "radius": 6 * mm});
            skLineSegment(sketch, "E91.MirrorCS", {"start": v(0, -90) * mm, "end": v(0, -120) * mm, "construction": true});
            skLineSegment(sketch, "E92.MirrorCS", {"start": v(-15, -108) * mm, "end": v(-15, -120) * mm});
            skLineSegment(sketch, "E93.MirrorCS", {"start": v(-33, -90) * mm, "end": v(-15, -108) * mm});
            skSolve(sketch);
        }
        {
            var Q0;
            Q0=makeQuery(id+"F16.imprint","IMPRINT",FACE,{"disambiguationData":[TD([[makeQuery(id+"F16.imprint","IMPRINT",EDGE,{"derivedFrom":makeQuery(id+"F1.opExtrude","CAP_EDGE",EDGE,{"disambiguationData":[OSD([sQuery(id+"F0.wireOp",EDGE,"E1.left")])],"isStart":true})}),-1.0]])]});
            var Q1;
            {var subQ0=sQuery(id+"F16.wireOp",EDGE,"E87.MirrorCS");Q1=makeQuery(id+"F16.imprint","IMPRINT",FACE,{"disambiguationData":[TD([[makeQuery(id+"F16.imprint","IMPRINT",EDGE,{"derivedFrom":subQ0}),1.0]])]});}
            var Q2;
            {var subQ0=sQuery(id+"F16.wireOp",EDGE,"E80");Q2=makeQuery(id+"F16.imprint","IMPRINT",FACE,{"disambiguationData":[TD([[makeQuery(id+"F16.imprint","IMPRINT",EDGE,{"derivedFrom":subQ0}),-1.0]])]});}
            extrude(context, id + "F17", {"entities" : qUnion([Q0, Q1, Q2]), "operationType" : NewBodyOperationType.ADD, "depth" : 25 * mm, "offsetDistance" : 25 * mm});
        }
    });
